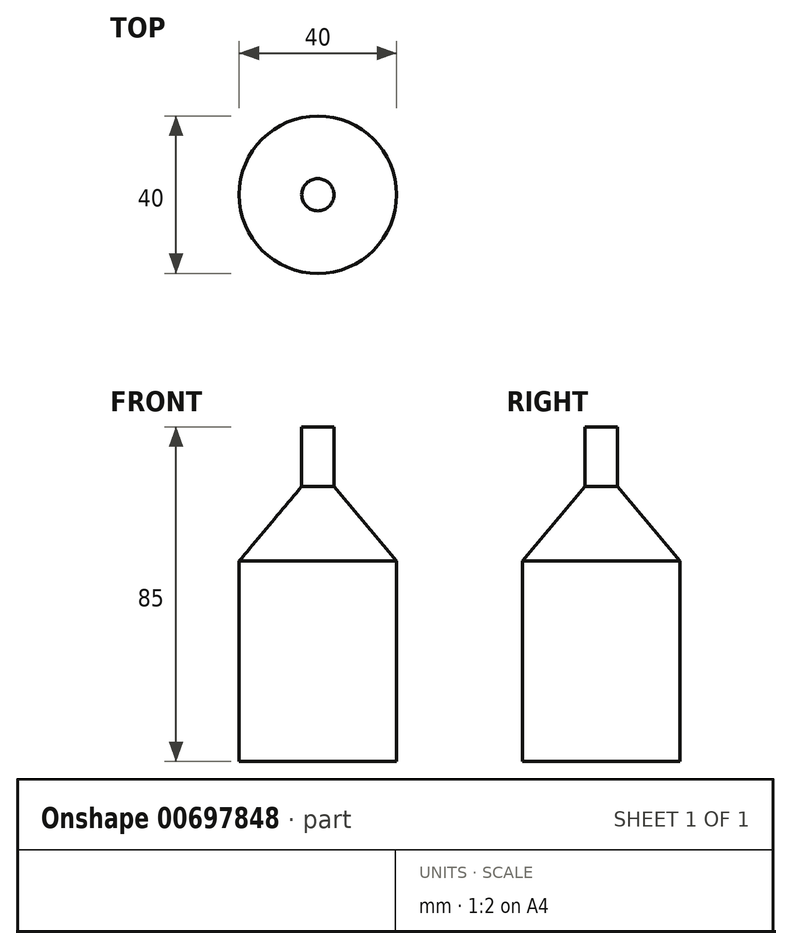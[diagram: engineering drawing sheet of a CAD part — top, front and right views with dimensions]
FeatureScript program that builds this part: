
annotation { "Feature Type Name" : "Feature", "Feature Type Description" : "" }
export const myFeature = defineFeature(function(context is Context, id is Id, definition is map)
    precondition{}
    {
        {
            var Q0;
            Q0=qCreatedBy(makeId("Top.planeOp"),FACE);
            var sketch = newSketch(context, id + "F0", { "sketchPlane" : qUnion([Q0])});
            skCircle(sketch, "E0", {"center": v(0, 0) * mm, "radius": 4.1 * mm});
            skSolve(sketch);
        }
        {
            var Q0;
            Q0 = qSketchRegion(id + "F0", true);
            extrude(context, id + "F1", {"entities" : qUnion([Q0]), "depth" : 15 * mm, "offsetDistance" : 25 * mm});
        }
        {
            var Q0;
            Q0=qCreatedBy(makeId("Top.planeOp"),FACE);
            var sketch = newSketch(context, id + "F2", { "sketchPlane" : qUnion([Q0])});
            skCircle(sketch, "E1", {"center": v(0, 0) * mm, "radius": 20 * mm});
            skSolve(sketch);
        }
        {
            var Q0;
            Q0 = qSketchRegion(id + "F2", true);
            extrude(context, id + "F3", {"entities" : qUnion([Q0]), "operationType" : NewBodyOperationType.ADD, "oppositeDirection" : true, "depth" : 70 * mm, "offsetDistance" : 25 * mm});
        }
        {
            var Q0;
            Q0=makeQuery(id+"F3.opExtrude","CAP_EDGE",EDGE,{"disambiguationData":[OSD([sQuery(id+"F2.wireOp",EDGE,"E1")])],"isStart":true});
            chamfer(context, id + "F4", {"entities" : qUnion([Q0]), "chamferType" : ChamferType.OFFSET_ANGLE, "width" : 16 * mm, "oppositeDirection" : false, "angle" : 50 * degree, "tangentPropagation" : true});
        }
    });
